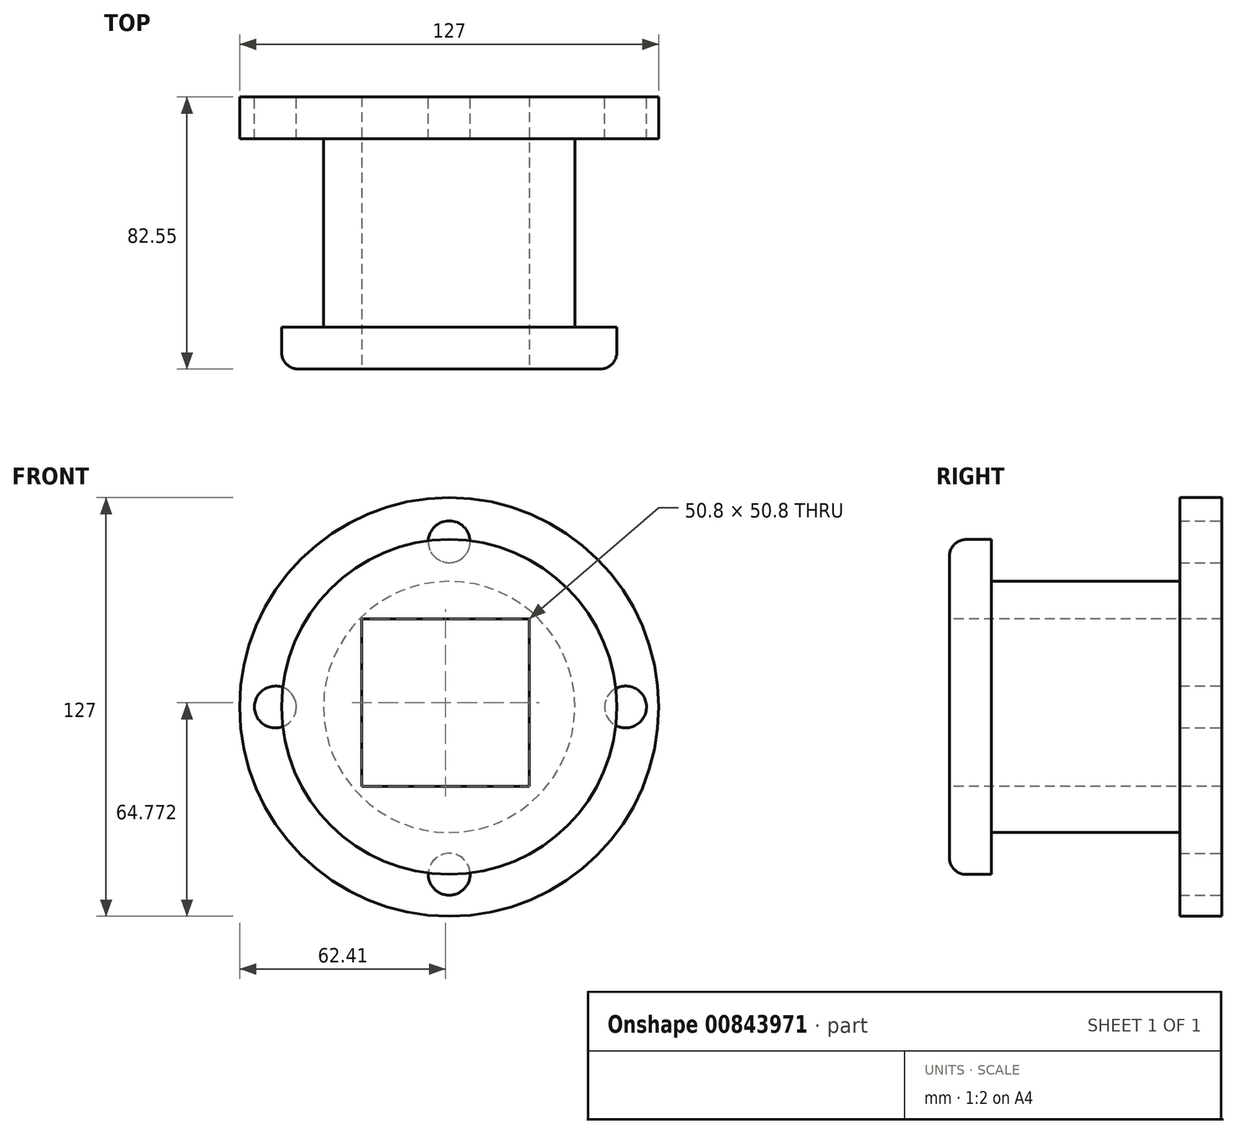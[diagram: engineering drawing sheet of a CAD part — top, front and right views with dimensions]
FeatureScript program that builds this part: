
annotation { "Feature Type Name" : "Feature", "Feature Type Description" : "" }
export const myFeature = defineFeature(function(context is Context, id is Id, definition is map)
    precondition{}
    {
        {
            var Q0;
            Q0=qCreatedBy(makeId("Front.planeOp"),FACE);
            var sketch = newSketch(context, id + "F0", { "sketchPlane" : qUnion([Q0])});
            skCircle(sketch, "E0", {"center": v(0, 0) * mm, "radius": 63.5 * mm});
            skCircle(sketch, "E1", {"center": v(0, 50.12) * mm, "radius": 6.35 * mm});
            skCircle(sketch, "E2", {"center": v(-52.7, 0) * mm, "radius": 6.35 * mm});
            skCircle(sketch, "E3", {"center": v(0, -50.74) * mm, "radius": 6.35 * mm});
            skCircle(sketch, "E4", {"center": v(53.47, 0) * mm, "radius": 6.35 * mm});
            skSolve(sketch);
        }
        {
            var Q0;
            Q0=makeQuery(id+"F0.imprint","IMPRINT",FACE,{"disambiguationData":[TD([[makeQuery(id+"F0.imprint","IMPRINT",EDGE,{"derivedFrom":sQuery(id+"F0.wireOp",EDGE,"E0")}),1.0]])]});
            extrude(context, id + "F1", {"entities" : qUnion([Q0]), "depth" : 12.7 * mm, "offsetDistance" : 25.4 * mm});
        }
        {
            var Q0;
            Q0=makeQuery(id+"F1.opExtrude","CAP_FACE",FACE,{"disambiguationData":[OSD([sQuery(id+"F0.wireOp",EDGE,"E0")])],"isStart":false});
            var sketch = newSketch(context, id + "F2", { "sketchPlane" : qUnion([Q0])});
            skCircle(sketch, "E5", {"center": v(0, 0) * mm, "radius": 38.1 * mm});
            skSolve(sketch);
        }
        {
            var Q0;
            Q0=makeQuery(id+"F2.imprint","IMPRINT",FACE,{"disambiguationData":[TD([[makeQuery(id+"F2.imprint","IMPRINT",EDGE,{"derivedFrom":sQuery(id+"F2.wireOp",EDGE,"E5")}),1.0]])]});
            extrude(context, id + "F3", {"entities" : qUnion([Q0]), "operationType" : NewBodyOperationType.ADD, "depth" : 57.15 * mm, "offsetDistance" : 25.4 * mm});
        }
        {
            var Q0;
            Q0=makeQuery(id+"F3.opExtrude","CAP_FACE",FACE,{"disambiguationData":[OSD([sQuery(id+"F2.wireOp",EDGE,"E5")])],"isStart":false});
            var sketch = newSketch(context, id + "F4", { "sketchPlane" : qUnion([Q0])});
            skCircle(sketch, "E6", {"center": v(0, 0) * mm, "radius": 50.8 * mm});
            skSolve(sketch);
        }
        {
            var Q0;
            Q0=makeQuery(id+"F4.imprint","IMPRINT",FACE,{"disambiguationData":[TD([[makeQuery(id+"F4.imprint","IMPRINT",EDGE,{"derivedFrom":makeQuery(id+"F3.opExtrude","CAP_EDGE",EDGE,{"disambiguationData":[OSD([sQuery(id+"F2.wireOp",EDGE,"E5")])],"isStart":false})}),1.0]])]});
            var Q1;
            Q1=makeQuery(id+"F4.imprint","IMPRINT",FACE,{"disambiguationData":[TD([[makeQuery(id+"F4.imprint","IMPRINT",EDGE,{"derivedFrom":sQuery(id+"F4.wireOp",EDGE,"E6")}),1.0]])]});
            extrude(context, id + "F5", {"entities" : qUnion([Q0, Q1]), "operationType" : NewBodyOperationType.ADD, "depth" : 12.7 * mm, "offsetDistance" : 25.4 * mm});
        }
        {
            var Q0;
            Q0=makeQuery(id+"F5.opExtrude","CAP_FACE",FACE,{"disambiguationData":[OSD([sQuery(id+"F4.wireOp",EDGE,"E6")])],"isStart":false});
            var sketch = newSketch(context, id + "F6", { "sketchPlane" : qUnion([Q0])});
            skLineSegment(sketch, "E7.bottom", {"start": v(24.3, -24.13) * mm, "end": v(-26.5, -24.13) * mm});
            skLineSegment(sketch, "E7.top", {"start": v(24.3, 26.67) * mm, "end": v(-26.5, 26.67) * mm});
            skLineSegment(sketch, "E7.left", {"start": v(24.3, -24.13) * mm, "end": v(24.3, 26.67) * mm});
            skLineSegment(sketch, "E7.right", {"start": v(-26.5, -24.13) * mm, "end": v(-26.5, 26.67) * mm});
            skSolve(sketch);
        }
        {
            var Q0;
            Q0=makeQuery(id+"F5.opExtrude","CAP_EDGE",EDGE,{"disambiguationData":[OSD([sQuery(id+"F4.wireOp",EDGE,"E6")])],"isStart":false});
            fillet(context, id + "F7", {"entities" : qUnion([Q0]), "radius" : 5.08 * mm, "tangentPropagation" : true, "allowEdgeOverflow" : false});
        }
        {
            var Q0;
            Q0 = qSketchRegion(id + "F6", true);
            extrude(context, id + "F8", {"entities" : qUnion([Q0]), "operationType" : NewBodyOperationType.REMOVE, "oppositeDirection" : true, "depth" : 101.6 * mm, "offsetDistance" : 25.4 * mm});
        }
    });
